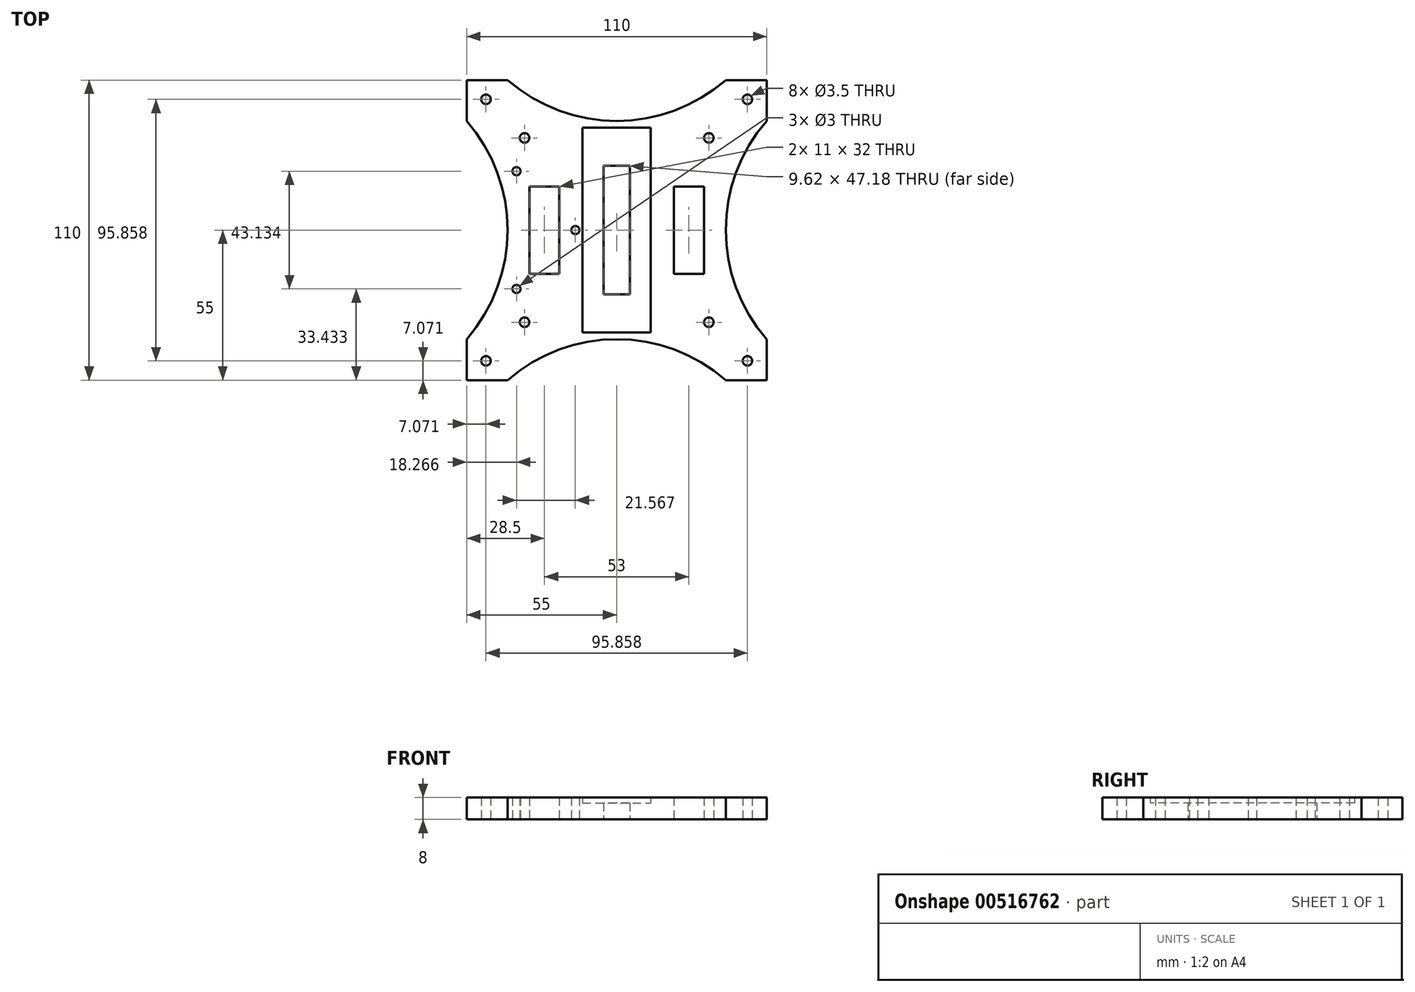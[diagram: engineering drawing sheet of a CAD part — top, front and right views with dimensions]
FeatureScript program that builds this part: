
annotation { "Feature Type Name" : "Feature", "Feature Type Description" : "" }
export const myFeature = defineFeature(function(context is Context, id is Id, definition is map)
    precondition{}
    {
        {
            var Q0;
            Q0=qCreatedBy(makeId("Top.planeOp"),FACE);
            var sketch = newSketch(context, id + "F0", { "sketchPlane" : qUnion([Q0])});
            skLineSegment(sketch, "E0.bottom", {"start": v(55, 55) * mm, "end": v(-55, 55) * mm});
            skLineSegment(sketch, "E0.top", {"start": v(55, -55) * mm, "end": v(-55, -55) * mm});
            skLineSegment(sketch, "E0.left", {"start": v(55, 55) * mm, "end": v(55, -55) * mm});
            skLineSegment(sketch, "E0.right", {"start": v(-55, 55) * mm, "end": v(-55, -55) * mm});
            skPoint(sketch, "E0.middle", {"position": v(0, 0) * mm});
            skCircle(sketch, "E1", {"center": v(-47.93, -47.93) * mm, "radius": 1.75 * mm});
            skCircle(sketch, "E2", {"center": v(-33.79, -33.79) * mm, "radius": 1.75 * mm});
            skCircle(sketch, "E3", {"center": v(47.93, -47.93) * mm, "radius": 1.75 * mm});
            skCircle(sketch, "E4", {"center": v(33.79, -33.79) * mm, "radius": 1.75 * mm});
            skCircle(sketch, "E5", {"center": v(47.93, 47.93) * mm, "radius": 1.75 * mm});
            skCircle(sketch, "E6", {"center": v(33.79, 33.79) * mm, "radius": 1.75 * mm});
            skCircle(sketch, "E7", {"center": v(-47.93, 47.93) * mm, "radius": 1.75 * mm});
            skCircle(sketch, "E8", {"center": v(-33.79, 33.79) * mm, "radius": 1.75 * mm});
            skLineSegment(sketch, "E9", {"start": v(-33.79, 33.79) * mm, "end": v(-55, 55) * mm});
            skLineSegment(sketch, "E10", {"start": v(33.79, 33.79) * mm, "end": v(55, 55) * mm});
            skLineSegment(sketch, "E11", {"start": v(33.79, -33.79) * mm, "end": v(55, -55) * mm});
            skLineSegment(sketch, "E12", {"start": v(-55, -55) * mm, "end": v(-33.79, -33.79) * mm});
            skLineSegment(sketch, "E13.bottom", {"start": v(-12.5, 37.5) * mm, "end": v(12.5, 37.5) * mm});
            skLineSegment(sketch, "E13.top", {"start": v(-12.5, -37.5) * mm, "end": v(12.5, -37.5) * mm});
            skLineSegment(sketch, "E13.left", {"start": v(-12.5, 37.5) * mm, "end": v(-12.5, -37.5) * mm});
            skLineSegment(sketch, "E13.right", {"start": v(12.5, 37.5) * mm, "end": v(12.5, -37.5) * mm});
            skLineSegment(sketch, "E14", {"start": v(-55, 0) * mm, "end": v(55, 0) * mm});
            skPoint(sketch, "E15.middle", {"position": v(27.87, 0) * mm});
            skArc(sketch, "E16", {"start": v(-55, -40) * mm, "mid": v(-40, 0) * mm, "end": v(-55, 40) * mm});
            skArc(sketch, "E17", {"start": v(-40, 55) * mm, "mid": v(0, 40) * mm, "end": v(40, 55) * mm});
            skArc(sketch, "E18", {"start": v(55, 40) * mm, "mid": v(40, 0) * mm, "end": v(55, -40) * mm});
            skArc(sketch, "E19", {"start": v(40, -55) * mm, "mid": v(0, -40) * mm, "end": v(-40, -55) * mm});
            skLineSegment(sketch, "E20", {"start": v(0, 55) * mm, "end": v(0, -55) * mm});
            skPoint(sketch, "E21", {"position": v(-40, 0) * mm});
            skCircle(sketch, "E22", {"center": v(-36.73, 21.57) * mm, "radius": 1.5 * mm});
            skLineSegment(sketch, "E23", {"start": v(-36.73, 21.57) * mm, "end": v(-36.73, -21.57) * mm});
            skCircle(sketch, "E24", {"center": v(-36.73, -21.57) * mm, "radius": 1.5 * mm});
            skCircle(sketch, "E25", {"center": v(-15.17, 0) * mm, "radius": 1.5 * mm});
            skLineSegment(sketch, "E26.bottom", {"start": v(4.81, 23.59) * mm, "end": v(-4.81, 23.59) * mm});
            skLineSegment(sketch, "E26.top", {"start": v(4.81, -23.59) * mm, "end": v(-4.81, -23.59) * mm});
            skLineSegment(sketch, "E26.left", {"start": v(4.81, 23.59) * mm, "end": v(4.81, -23.59) * mm});
            skLineSegment(sketch, "E26.right", {"start": v(-4.81, 23.59) * mm, "end": v(-4.81, -23.59) * mm});
            skLineSegment(sketch, "E27.bottom", {"start": v(-21, 16) * mm, "end": v(-32, 16) * mm});
            skLineSegment(sketch, "E27.top", {"start": v(-21, -16) * mm, "end": v(-32, -16) * mm});
            skLineSegment(sketch, "E27.left", {"start": v(-21, 16) * mm, "end": v(-21, -16) * mm});
            skLineSegment(sketch, "E27.right", {"start": v(-32, 16) * mm, "end": v(-32, -16) * mm});
            skPoint(sketch, "E27.middle", {"position": v(-26.5, 0) * mm});
            skLineSegment(sketch, "E28.bottom", {"start": v(32, 16) * mm, "end": v(21, 16) * mm});
            skLineSegment(sketch, "E28.top", {"start": v(32, -16) * mm, "end": v(21, -16) * mm});
            skLineSegment(sketch, "E28.left", {"start": v(32, 16) * mm, "end": v(32, -16) * mm});
            skLineSegment(sketch, "E28.right", {"start": v(21, 16) * mm, "end": v(21, -16) * mm});
            skPoint(sketch, "E28.middle", {"position": v(26.5, 0) * mm});
            skSolve(sketch);
        }
        {
            var Q0;
            Q0=makeQuery(id+"F0.imprint","IMPRINT",FACE,{"disambiguationData":[TD([[makeQuery(id+"F0.imprint","IMPRINT",EDGE,{"derivedFrom":sQuery(id+"F0.wireOp",EDGE,"E6")}),-1.0]])]});
            var Q1;
            Q1=makeQuery(id+"F0.imprint","IMPRINT",FACE,{"disambiguationData":[TD([[makeQuery(id+"F0.imprint","IMPRINT",EDGE,{"derivedFrom":sQuery(id+"F0.wireOp",EDGE,"E2")}),-1.0]])]});
            var Q2;
            Q2=makeQuery(id+"F0.imprint","IMPRINT",FACE,{"disambiguationData":[TD([[makeQuery(id+"F0.imprint","IMPRINT",EDGE,{"derivedFrom":sQuery(id+"F0.wireOp",EDGE,"E8")}),-1.0]])]});
            var Q3;
            Q3=makeQuery(id+"F0.imprint","IMPRINT",FACE,{"disambiguationData":[TD([[makeQuery(id+"F0.imprint","IMPRINT",EDGE,{"derivedFrom":sQuery(id+"F0.wireOp",EDGE,"E4")}),-1.0]])]});
            var Q4;
            Q4=makeQuery(id+"F0.imprint","IMPRINT",FACE,{"disambiguationData":[TD([[makeQuery(id+"F0.imprint","IMPRINT",EDGE,{"derivedFrom":sQuery(id+"F0.wireOp",EDGE,"8edccc17-94d5-44be-8713-b707545185b8")}),-1.0]])]});
            var Q5;
            Q5=makeQuery(id+"F0.imprint","IMPRINT",FACE,{"disambiguationData":[TD([[makeQuery(id+"F0.imprint","IMPRINT",EDGE,{"derivedFrom":sQuery(id+"F0.wireOp",EDGE,"5aa0522a-8e5d-442c-aa93-86395ba26cf6")}),-1.0]])]});
            var Q6;
            Q6=makeQuery(id+"F0.imprint","IMPRINT",FACE,{"disambiguationData":[TD([[makeQuery(id+"F0.imprint","IMPRINT",EDGE,{"derivedFrom":sQuery(id+"F0.wireOp",EDGE,"d934e56b-7aaa-40aa-869f-8220faf7eb30")}),-1.0]])]});
            var Q7;
            Q7=makeQuery(id+"F0.imprint","IMPRINT",FACE,{"disambiguationData":[TD([[makeQuery(id+"F0.imprint","IMPRINT",EDGE,{"derivedFrom":sQuery(id+"F0.wireOp",EDGE,"9eefc30d-1561-4254-a589-462d371f82b0")}),-1.0]])]});
            extrude(context, id + "F1", {"entities" : qUnion([Q0, Q1, Q2, Q3, Q4, Q5, Q6, Q7]), "depth" : 8 * mm, "offsetDistance" : 25 * mm, "symmetric" : true});
        }
        {
            var Q0;
            {var subQ0=sQuery(id+"F0.wireOp",EDGE,"E13.top");Q0=makeQuery(id+"F0.imprint","IMPRINT",FACE,{"disambiguationData":[TD([[makeQuery(id+"F0.imprint","IMPRINT",EDGE,{"derivedFrom":subQ0}),1.0]])]});}
            var Q1;
            {var subQ0=sQuery(id+"F0.wireOp",EDGE,"E13.bottom");Q1=makeQuery(id+"F0.imprint","IMPRINT",FACE,{"disambiguationData":[TD([[makeQuery(id+"F0.imprint","IMPRINT",EDGE,{"derivedFrom":subQ0}),-1.0]])]});}
            extrude(context, id + "F2", {"entities" : qUnion([Q0, Q1]), "operationType" : NewBodyOperationType.ADD, "depth" : 4 * mm, "offsetDistance" : 25 * mm, "symmetric" : true});
        }
        {
            var Q0;
            {var subQ0=sQuery(id+"F0.wireOp",EDGE,"E13.top");Q0=makeQuery(id+"F0.imprint","IMPRINT",FACE,{"disambiguationData":[TD([[makeQuery(id+"F0.imprint","IMPRINT",EDGE,{"derivedFrom":subQ0}),1.0]])]});}
            var Q1;
            {var subQ0=sQuery(id+"F0.wireOp",EDGE,"E13.bottom");Q1=makeQuery(id+"F0.imprint","IMPRINT",FACE,{"disambiguationData":[TD([[makeQuery(id+"F0.imprint","IMPRINT",EDGE,{"derivedFrom":subQ0}),-1.0]])]});}
            extrude(context, id + "F3", {"entities" : qUnion([Q0, Q1]), "operationType" : NewBodyOperationType.ADD, "oppositeDirection" : true, "depth" : 4 * mm});
        }
    });
